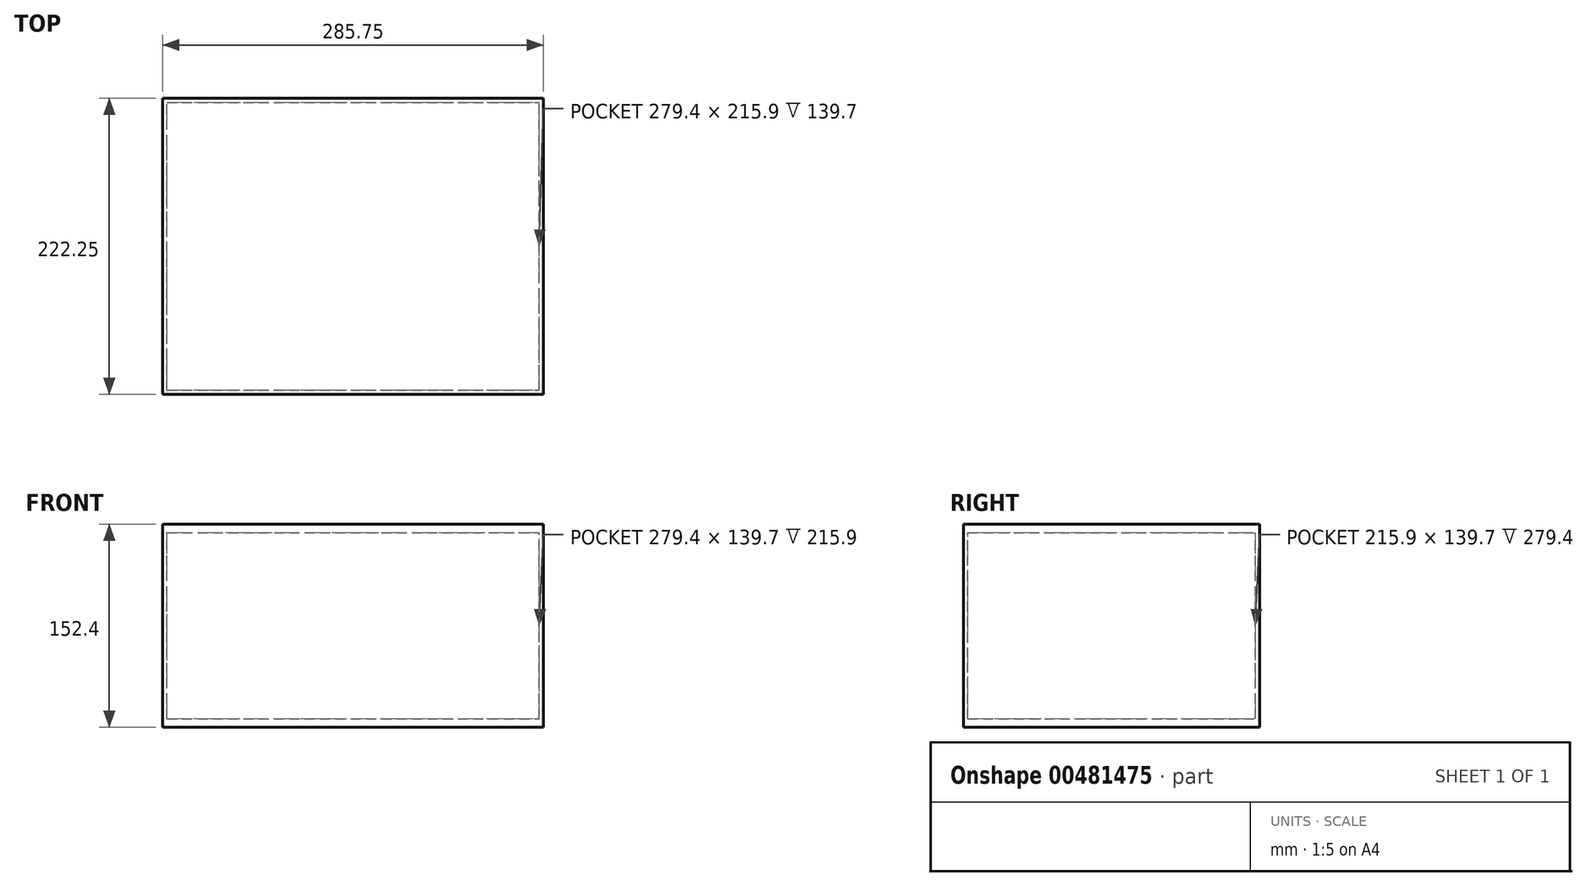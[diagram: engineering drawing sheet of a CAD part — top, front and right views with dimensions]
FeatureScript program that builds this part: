
annotation { "Feature Type Name" : "Feature", "Feature Type Description" : "" }
export const myFeature = defineFeature(function(context is Context, id is Id, definition is map)
    precondition{}
    {
        {
            var Q0;
            Q0=qCreatedBy(makeId("Top.planeOp"),FACE);
            var sketch = newSketch(context, id + "F0", { "sketchPlane" : qUnion([Q0])});
            skLineSegment(sketch, "E0.bottom", {"start": v(0, 0) * mm, "end": v(285.75, 0) * mm});
            skLineSegment(sketch, "E0.top", {"start": v(0, 222.25) * mm, "end": v(285.75, 222.25) * mm});
            skLineSegment(sketch, "E0.left", {"start": v(0, 0) * mm, "end": v(0, 222.25) * mm});
            skLineSegment(sketch, "E0.right", {"start": v(285.75, 0) * mm, "end": v(285.75, 222.25) * mm});
            skSolve(sketch);
        }
        {
            var Q0;
            Q0 = qSketchRegion(id + "F0", true);
            extrude(context, id + "F1", {"entities" : qUnion([Q0]), "endBound" : BoundingType.SYMMETRIC, "oppositeDirection" : true, "depth" : 152.4 * mm});
        }
        {
            var Q0;
            Q0=qCreatedBy(makeId("Top.planeOp"),FACE);
            var sketch = newSketch(context, id + "F2", { "sketchPlane" : qUnion([Q0])});
            skLineSegment(sketch, "E1.bottom", {"start": v(3.17, 3.18) * mm, "end": v(282.58, 3.18) * mm});
            skLineSegment(sketch, "E1.top", {"start": v(3.17, 219.07) * mm, "end": v(282.58, 219.07) * mm});
            skLineSegment(sketch, "E1.left", {"start": v(3.17, 3.18) * mm, "end": v(3.17, 219.07) * mm});
            skLineSegment(sketch, "E1.right", {"start": v(282.58, 3.18) * mm, "end": v(282.57, 219.07) * mm});
            skSolve(sketch);
        }
        {
            var Q0;
            Q0 = qSketchRegion(id + "F2", true);
            extrude(context, id + "F3", {"entities" : qUnion([Q0]), "operationType" : NewBodyOperationType.REMOVE, "endBound" : BoundingType.SYMMETRIC, "oppositeDirection" : true, "depth" : 139.7 * mm});
        }
    });
